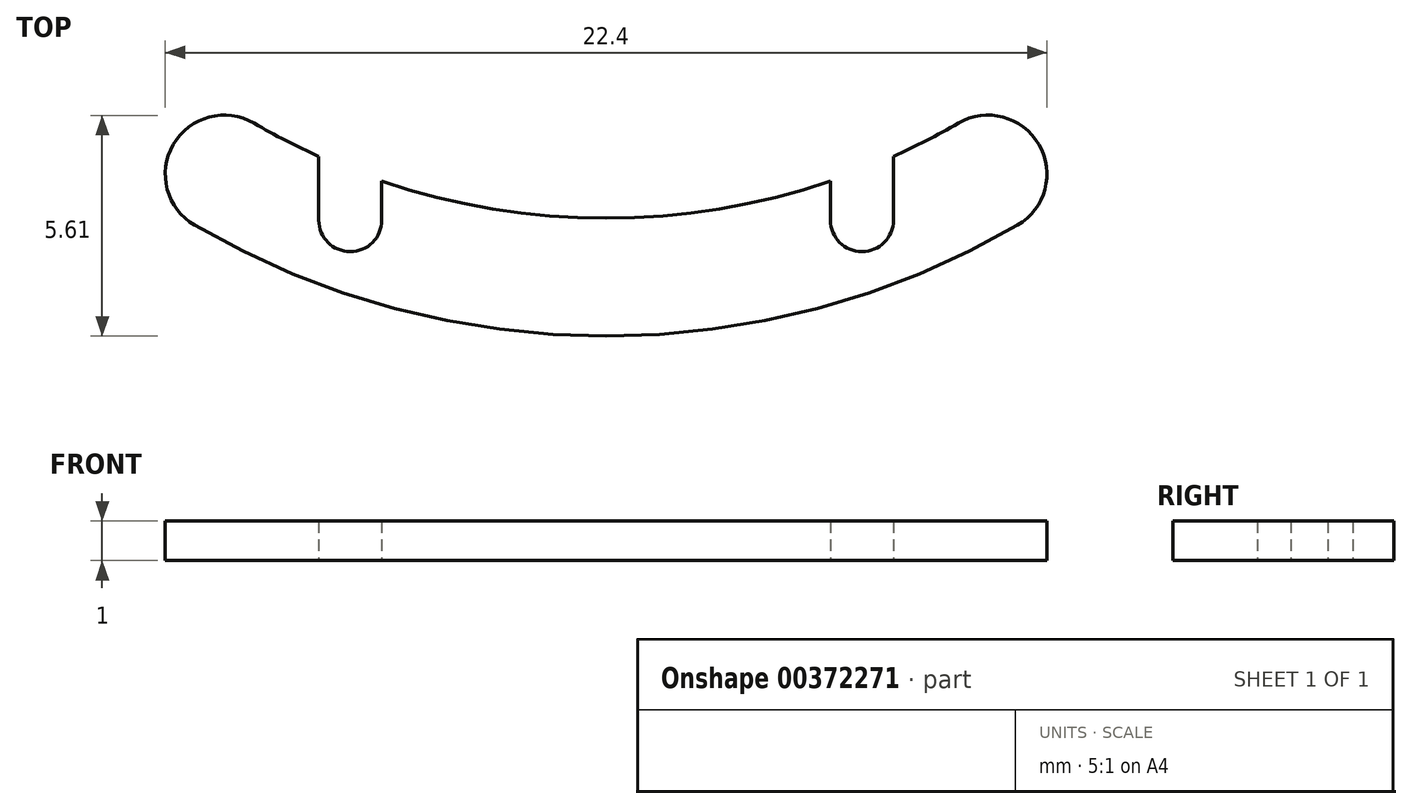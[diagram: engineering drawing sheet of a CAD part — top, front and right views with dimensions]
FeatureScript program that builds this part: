
annotation { "Feature Type Name" : "Feature", "Feature Type Description" : "" }
export const myFeature = defineFeature(function(context is Context, id is Id, definition is map)
    precondition{}
    {
        {
            var Q0;
            Q0=qCreatedBy(makeId("Top.planeOp"),FACE);
            var sketch = newSketch(context, id + "F0", { "sketchPlane" : qUnion([Q0])});
            skArc(sketch, "E0", {"start": v(-8.95, -15.39) * mm, "mid": v(-8.13, -15.83) * mm, "end": v(-7.3, -16.23) * mm});
            skCircle(sketch, "E1", {"center": v(0, 0) * mm, "radius": 19 * mm, "construction": true});
            skArc(sketch, "E2", {"start": v(-10.45, -17.98) * mm, "mid": v(0, -20.8) * mm, "end": v(10.45, -17.98) * mm});
            skArc(sketch, "E3", {"start": v(-8.95, -15.39) * mm, "mid": v(-11, -15.93) * mm, "end": v(-10.45, -17.98) * mm});
            skArc(sketch, "E4", {"start": v(10.45, -17.98) * mm, "mid": v(11, -15.93) * mm, "end": v(8.95, -15.39) * mm});
            skArc(sketch, "E5", {"start": v(-7.3, -17.85) * mm, "mid": v(-6.5, -18.65) * mm, "end": v(-5.7, -17.85) * mm});
            skArc(sketch, "E6", {"start": v(5.7, -17.85) * mm, "mid": v(6.5, -18.65) * mm, "end": v(7.3, -17.85) * mm});
            skLineSegment(sketch, "E7", {"start": v(-7.3, -17.85) * mm, "end": v(-7.3, -16.23) * mm});
            skLineSegment(sketch, "E8", {"start": v(-5.7, -17.85) * mm, "end": v(-5.7, -16.86) * mm});
            skLineSegment(sketch, "E9", {"start": v(5.7, -17.85) * mm, "end": v(5.7, -16.86) * mm});
            skLineSegment(sketch, "E10", {"start": v(7.3, -17.85) * mm, "end": v(7.3, -16.23) * mm});
            skArc(sketch, "E11.trimOffspring", {"start": v(-5.7, -16.86) * mm, "mid": v(0, -17.8) * mm, "end": v(5.7, -16.86) * mm});
            skArc(sketch, "E12.trimOffspring", {"start": v(7.3, -16.23) * mm, "mid": v(8.13, -15.83) * mm, "end": v(8.95, -15.39) * mm});
            skSolve(sketch);
        }
        {
            var Q0;
            Q0=makeQuery(id+"F0.imprint","IMPRINT",FACE,{"disambiguationData":[TD([[makeQuery(id+"F0.imprint","IMPRINT",EDGE,{"derivedFrom":sQuery(id+"F0.wireOp",EDGE,"E0")}),-1.0]])]});
            extrude(context, id + "F1", {"entities" : qUnion([Q0]), "depth" : 1 * mm});
        }
    });
